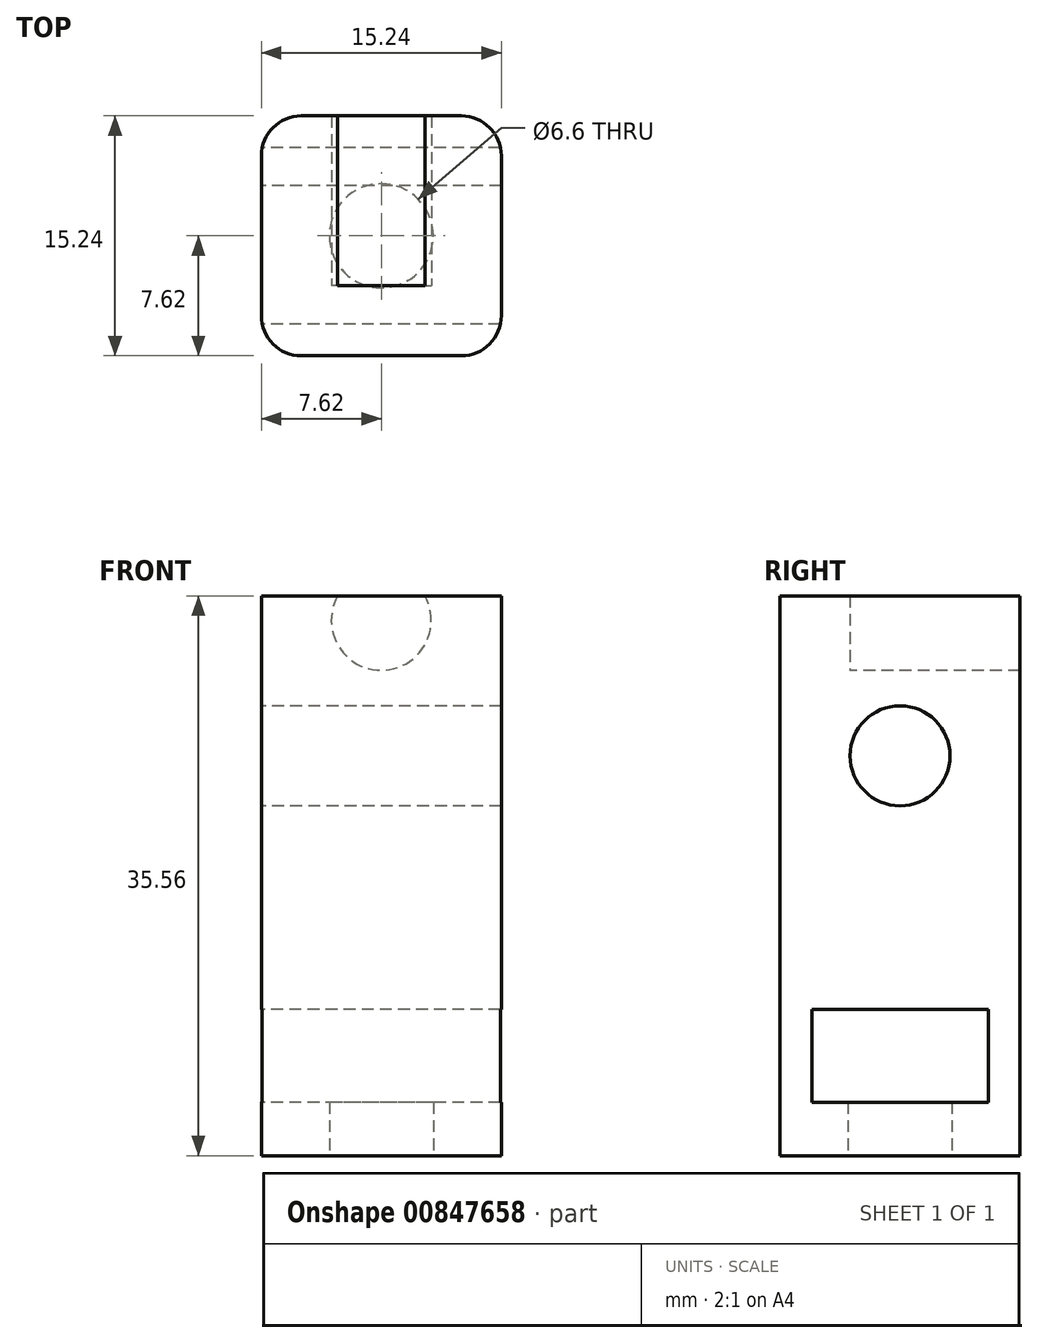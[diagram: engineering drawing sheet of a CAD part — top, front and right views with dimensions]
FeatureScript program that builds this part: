
annotation { "Feature Type Name" : "Feature", "Feature Type Description" : "" }
export const myFeature = defineFeature(function(context is Context, id is Id, definition is map)
    precondition{}
    {
        {
            var Q0;
            Q0=qCreatedBy(makeId("Top.planeOp"),FACE);
            var sketch = newSketch(context, id + "F0", { "sketchPlane" : qUnion([Q0])});
            skLineSegment(sketch, "E0.bottom", {"start": v(7.62, -7.62) * mm, "end": v(-7.62, -7.62) * mm});
            skLineSegment(sketch, "E0.top", {"start": v(7.62, 7.62) * mm, "end": v(-7.62, 7.62) * mm});
            skLineSegment(sketch, "E0.left", {"start": v(7.62, -7.62) * mm, "end": v(7.62, 7.62) * mm});
            skLineSegment(sketch, "E0.right", {"start": v(-7.62, -7.62) * mm, "end": v(-7.62, 7.62) * mm});
            skPoint(sketch, "E0.middle", {"position": v(0, 0) * mm});
            skSolve(sketch);
        }
        {
            var Q0;
            Q0 = qSketchRegion(id + "F0", true);
            extrude(context, id + "F1", {"entities" : qUnion([Q0]), "depth" : 35.56 * mm, "offsetDistance" : 25.4 * mm});
        }
        {
            var Q0;
            Q0=qCreatedBy(makeId("Front.planeOp"),FACE);
            var sketch = newSketch(context, id + "F2", { "sketchPlane" : qUnion([Q0])});
            skCircle(sketch, "E1", {"center": v(0, 34) * mm, "radius": 3.18 * mm});
            skLineSegment(sketch, "E2.0", {"start": v(7.62, 35.56) * mm, "end": v(-7.62, 35.56) * mm, "construction": true});
            skSolve(sketch);
        }
        {
            var Q0;
            {var subQ0=sQuery(id+"F2.wireOp",EDGE,"E2.0");var subQ1=sQuery(id+"F2.wireOp",EDGE,"E1");var subQ2=makeQuery(id+"F2.imprint","INTERSECT",VERTEX,{"disambiguationData":[OD(0.0)],"derivedFrom":[subQ1,subQ0]});Q0=makeQuery(id+"F2.imprint","IMPRINT",FACE,{"disambiguationData":[TD([[makeQuery(id+"F2.imprint","IMPRINT",EDGE,{"disambiguationData":[TD([[subQ2,1.0]])],"derivedFrom":subQ1}),1.0]])]});}
            extrude(context, id + "F3", {"entities" : qUnion([Q0]), "operationType" : NewBodyOperationType.REMOVE, "oppositeDirection" : true, "depth" : 12.7 * mm, "offsetDistance" : 25.4 * mm, "hasSecondDirection" : true, "secondDirectionOppositeDirection" : false, "secondDirectionDepth" : 3.17 * mm});
        }
        {
            var Q0;
            Q0=qCreatedBy(makeId("Right.planeOp"),FACE);
            var sketch = newSketch(context, id + "F4", { "sketchPlane" : qUnion([Q0])});
            skCircle(sketch, "E3", {"center": v(0, 25.4) * mm, "radius": 3.18 * mm});
            skLineSegment(sketch, "E4.bottom", {"start": v(-5.6, 3.4) * mm, "end": v(5.6, 3.4) * mm});
            skLineSegment(sketch, "E4.top", {"start": v(-5.6, 9.3) * mm, "end": v(5.6, 9.3) * mm});
            skLineSegment(sketch, "E4.left", {"start": v(-5.6, 3.4) * mm, "end": v(-5.6, 9.3) * mm});
            skLineSegment(sketch, "E4.right", {"start": v(5.6, 3.4) * mm, "end": v(5.6, 9.3) * mm});
            skPoint(sketch, "E4.middle", {"position": v(0, 6.35) * mm});
            skSolve(sketch);
        }
        {
            var Q0;
            Q0 = qSketchRegion(id + "F4", true);
            extrude(context, id + "F5", {"entities" : qUnion([Q0]), "operationType" : NewBodyOperationType.REMOVE, "endBound" : BoundingType.SYMMETRIC, "depth" : 25.4 * mm, "offsetDistance" : 25.4 * mm});
        }
        {
            var Q0;
            Q0=makeQuery(id+"F1.opExtrude","SWEPT_EDGE",EDGE,{"disambiguationData":[OSD([sQuery(id+"F0.wireOp",EDGE,"E0.top"),sQuery(id+"F0.wireOp",EDGE,"E0.left")])]});
            var Q1;
            Q1=makeQuery(id+"F1.opExtrude","SWEPT_EDGE",EDGE,{"disambiguationData":[OSD([sQuery(id+"F0.wireOp",EDGE,"E0.bottom"),sQuery(id+"F0.wireOp",EDGE,"E0.left")])]});
            var Q2;
            Q2=makeQuery(id+"F1.opExtrude","SWEPT_EDGE",EDGE,{"disambiguationData":[OSD([sQuery(id+"F0.wireOp",EDGE,"E0.top"),sQuery(id+"F0.wireOp",EDGE,"E0.right")])]});
            var Q3;
            Q3=makeQuery(id+"F1.opExtrude","SWEPT_EDGE",EDGE,{"disambiguationData":[OSD([sQuery(id+"F0.wireOp",EDGE,"E0.bottom"),sQuery(id+"F0.wireOp",EDGE,"E0.right")])]});
            fillet(context, id + "F6", {"entities" : qUnion([Q0, Q1, Q2, Q3]), "radius" : 2.54 * mm, "tangentPropagation" : true, "allowEdgeOverflow" : false});
        }
        {
            var Q0;
            Q0=makeQuery(id+"F1.opExtrude","CAP_FACE",FACE,{"disambiguationData":[OSD([sQuery(id+"F0.wireOp",EDGE,"E0.bottom"),sQuery(id+"F0.wireOp",EDGE,"E0.top"),sQuery(id+"F0.wireOp",EDGE,"E0.left"),sQuery(id+"F0.wireOp",EDGE,"E0.right")])],"isStart":true});
            var sketch = newSketch(context, id + "F7", { "sketchPlane" : qUnion([Q0])});
            skCircle(sketch, "E5", {"center": v(0, 0) * mm, "radius": 3.3 * mm});
            skSolve(sketch);
        }
        {
            var Q0;
            Q0 = qSketchRegion(id + "F7", true);
            extrude(context, id + "F8", {"entities" : qUnion([Q0]), "operationType" : NewBodyOperationType.REMOVE, "oppositeDirection" : true, "depth" : 6.35 * mm, "offsetDistance" : 25.4 * mm});
        }
    });
